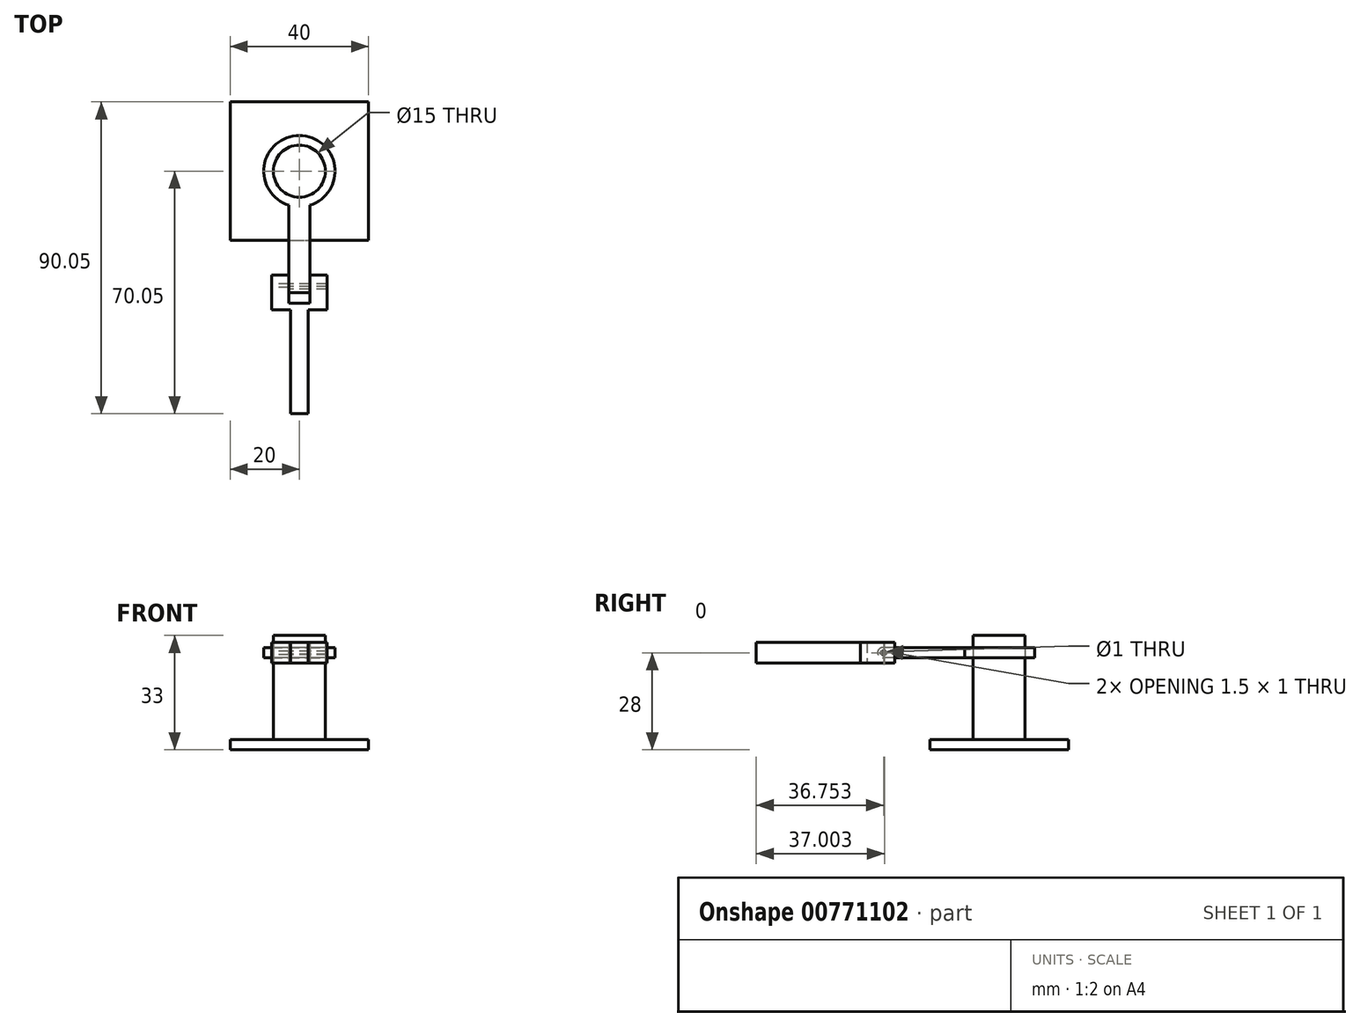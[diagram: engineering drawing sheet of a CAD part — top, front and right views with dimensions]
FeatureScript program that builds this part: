
annotation { "Feature Type Name" : "Feature", "Feature Type Description" : "" }
export const myFeature = defineFeature(function(context is Context, id is Id, definition is map)
    precondition{}
    {
        {
            var Q0;
            Q0=qCreatedBy(makeId("Top.planeOp"),FACE);
            var sketch = newSketch(context, id + "F0", { "sketchPlane" : qUnion([Q0])});
            skLineSegment(sketch, "E0.bottom", {"start": v(-20, 20) * mm, "end": v(20, 20) * mm});
            skLineSegment(sketch, "E0.top", {"start": v(-20, -20) * mm, "end": v(20, -20) * mm});
            skLineSegment(sketch, "E0.left", {"start": v(-20, 20) * mm, "end": v(-20, -20) * mm});
            skLineSegment(sketch, "E0.right", {"start": v(20, 20) * mm, "end": v(20, -20) * mm});
            skSolve(sketch);
        }
        {
            var Q0;
            Q0=makeQuery(id+"F0.imprint","IMPRINT",FACE,{"disambiguationData":[TD([[makeQuery(id+"F0.imprint","IMPRINT",EDGE,{"derivedFrom":sQuery(id+"F0.wireOp",EDGE,"E0.bottom")}),-1.0]])]});
            extrude(context, id + "F1", {"entities" : qUnion([Q0]), "depth" : -3 * mm, "offsetDistance" : 25 * mm});
        }
        {
            var Q0;
            Q0=makeQuery(id+"F1.opExtrude","CAP_FACE",FACE,{"disambiguationData":[OSD([sQuery(id+"F0.wireOp",EDGE,"E0.bottom"),sQuery(id+"F0.wireOp",EDGE,"E0.top"),sQuery(id+"F0.wireOp",EDGE,"E0.left"),sQuery(id+"F0.wireOp",EDGE,"E0.right")])],"isStart":true});
            var sketch = newSketch(context, id + "F2", { "sketchPlane" : qUnion([Q0])});
            skCircle(sketch, "E1", {"center": v(0, 0) * mm, "radius": 7.5 * mm});
            skSolve(sketch);
        }
        {
            var Q0;
            Q0=makeQuery(id+"F2.imprint","IMPRINT",FACE,{"disambiguationData":[TD([[makeQuery(id+"F2.imprint","IMPRINT",EDGE,{"derivedFrom":sQuery(id+"F2.wireOp",EDGE,"E1")}),1.0]])]});
            extrude(context, id + "F3", {"entities" : qUnion([Q0]), "depth" : 30 * mm, "offsetDistance" : 25 * mm});
        }
        {
            var Q0;
            Q0=qCreatedBy(makeId("Top.planeOp"),FACE);
            cPlane(context, id + "F4", {"entities" : qUnion([Q0]), "cplaneType" : CPlaneType.OFFSET, "offset" : 25 * mm, "width" : 150 * mm, "height" : 150 * mm});
        }
        {
            var Q0;
            Q0=qCreatedBy(id+"F4.planeOp",FACE);
            var sketch = newSketch(context, id + "F5", { "sketchPlane" : qUnion([Q0])});
            skCircle(sketch, "E2", {"center": v(0, 0) * mm, "radius": 7.5 * mm});
            skLineSegment(sketch, "E3", {"start": v(0, 0) * mm, "end": v(0, -15.37) * mm, "construction": true});
            skArc(sketch, "E4", {"start": v(3, -9.85) * mm, "mid": v(0, 10.3) * mm, "end": v(-3, -9.85) * mm});
            skLineSegment(sketch, "E5.top", {"start": v(-3, -35.05) * mm, "end": v(3, -35.05) * mm});
            skLineSegment(sketch, "E5.left", {"start": v(-3, -9.85) * mm, "end": v(-3, -35.05) * mm});
            skPoint(sketch, "E6.orphan", {"position": v(-3, 0) * mm});
            skLineSegment(sketch, "E7.trimOffspring", {"start": v(3, -9.85) * mm, "end": v(3, -35.05) * mm});
            skSolve(sketch);
        }
        {
            var Q0;
            Q0=makeQuery(id+"F5.imprint","IMPRINT",FACE,{"disambiguationData":[TD([[makeQuery(id+"F5.imprint","IMPRINT",EDGE,{"derivedFrom":sQuery(id+"F5.wireOp",EDGE,"E2")}),-1.0]])]});
            extrude(context, id + "F6", {"entities" : qUnion([Q0]), "endBound" : BoundingType.SYMMETRIC, "depth" : -3 * mm, "offsetDistance" : 25 * mm});
        }
        {
            var Q0;
            Q0=qCreatedBy(id+"F4.planeOp",FACE);
            var sketch = newSketch(context, id + "F7", { "sketchPlane" : qUnion([Q0])});
            skLineSegment(sketch, "E8.0", {"start": v(-3, -9.85) * mm, "end": v(-3, -35.05) * mm});
            skLineSegment(sketch, "E9.0", {"start": v(-3, -35.05) * mm, "end": v(3, -35.05) * mm});
            skLineSegment(sketch, "E10.0", {"start": v(3, -9.85) * mm, "end": v(3, -35.05) * mm});
            skLineSegment(sketch, "E11.bottom", {"start": v(-8, -30.05) * mm, "end": v(-3, -30.05) * mm});
            skLineSegment(sketch, "E11.top", {"start": v(-8, -40.05) * mm, "end": v(-2.5, -40.05) * mm});
            skLineSegment(sketch, "E11.left", {"start": v(-8, -30.05) * mm, "end": v(-8, -40.05) * mm});
            skLineSegment(sketch, "E11.right", {"start": v(8, -30.05) * mm, "end": v(8, -40.05) * mm});
            skLineSegment(sketch, "E12", {"start": v(-3, -30.05) * mm, "end": v(-3, -38.12) * mm});
            skLineSegment(sketch, "E13", {"start": v(-3, -38.12) * mm, "end": v(3, -38.12) * mm});
            skLineSegment(sketch, "E14", {"start": v(3, -38.12) * mm, "end": v(3, -30.05) * mm});
            skLineSegment(sketch, "E15.trimOffspring", {"start": v(-3, -30.05) * mm, "end": v(3, -30.05) * mm});
            skLineSegment(sketch, "E16.trimOffspring", {"start": v(3, -30.05) * mm, "end": v(8, -30.05) * mm});
            skLineSegment(sketch, "E17.top", {"start": v(-2.5, -70.05) * mm, "end": v(2.5, -70.05) * mm});
            skLineSegment(sketch, "E17.left", {"start": v(-2.5, -40.05) * mm, "end": v(-2.5, -70.05) * mm});
            skLineSegment(sketch, "E17.right", {"start": v(2.5, -40.05) * mm, "end": v(2.5, -70.05) * mm});
            skLineSegment(sketch, "E18.trimOffspring", {"start": v(2.5, -40.05) * mm, "end": v(8, -40.05) * mm});
            skSolve(sketch);
        }
        {
            var Q0;
            Q0=makeQuery(id+"F7.imprint","IMPRINT",FACE,{"disambiguationData":[TD([[makeQuery(id+"F7.imprint","IMPRINT",EDGE,{"derivedFrom":sQuery(id+"F7.wireOp",EDGE,"E11.bottom")}),-1.0]])]});
            extrude(context, id + "F8", {"entities" : qUnion([Q0]), "endBound" : BoundingType.SYMMETRIC, "depth" : 6 * mm, "offsetDistance" : 25 * mm});
        }
        {
            var Q0;
            Q0=makeQuery(id+"F6.opExtrude","CAP_EDGE",EDGE,{"disambiguationData":[OSD([sQuery(id+"F5.wireOp",EDGE,"E5.top")])],"isStart":false});
            var Q1;
            Q1=makeQuery(id+"F6.opExtrude","CAP_EDGE",EDGE,{"disambiguationData":[OSD([sQuery(id+"F5.wireOp",EDGE,"E5.top")])],"isStart":true});
            fillet(context, id + "F9", {"entities" : qUnion([Q0, Q1]), "radius" : 1.5 * mm, "tangentPropagation" : true, "allowEdgeOverflow" : false});
        }
        {
            var Q0;
            Q0=makeQuery(id+"F6.opExtrude","SWEPT_FACE",FACE,{"disambiguationData":[OSD([sQuery(id+"F5.wireOp",EDGE,"E5.left")])]});
            var sketch = newSketch(context, id + "F10", { "sketchPlane" : qUnion([Q0])});
            skPoint(sketch, "E19.0", {"position": v(35.05, 25) * mm});
            skCircle(sketch, "E20", {"center": v(33.55, 25) * mm, "radius": 0.5 * mm});
            skSolve(sketch);
        }
        {
            var Q0;
            Q0=makeQuery(id+"F10.imprint","IMPRINT",FACE,{"disambiguationData":[TD([[makeQuery(id+"F10.imprint","IMPRINT",EDGE,{"derivedFrom":sQuery(id+"F10.wireOp",EDGE,"E20")}),1.0]])]});
            extrude(context, id + "F11", {"entities" : qUnion([Q0]), "operationType" : NewBodyOperationType.REMOVE, "endBound" : BoundingType.THROUGH_ALL, "oppositeDirection" : true, "depth" : 25 * mm, "offsetDistance" : 25 * mm});
        }
        {
            var Q0;
            Q0=makeQuery(id+"F8.opExtrude","SWEPT_FACE",FACE,{"disambiguationData":[OSD([sQuery(id+"F7.wireOp",EDGE,"E11.left")])]});
            var sketch = newSketch(context, id + "F12", { "sketchPlane" : qUnion([Q0])});
            skCircle(sketch, "E21", {"center": v(33.05, 25) * mm, "radius": 0.5 * mm});
            skPoint(sketch, "E21.centerSnap0", {"position": v(30.05, 25) * mm});
            skSolve(sketch);
        }
        {
            var Q0;
            Q0=makeQuery(id+"F12.imprint","IMPRINT",FACE,{"disambiguationData":[TD([[makeQuery(id+"F12.imprint","IMPRINT",EDGE,{"derivedFrom":sQuery(id+"F12.wireOp",EDGE,"E21")}),1.0]])]});
            extrude(context, id + "F13", {"entities" : qUnion([Q0]), "operationType" : NewBodyOperationType.REMOVE, "endBound" : BoundingType.THROUGH_ALL, "oppositeDirection" : true, "depth" : 25 * mm, "offsetDistance" : 25 * mm});
        }
    });
